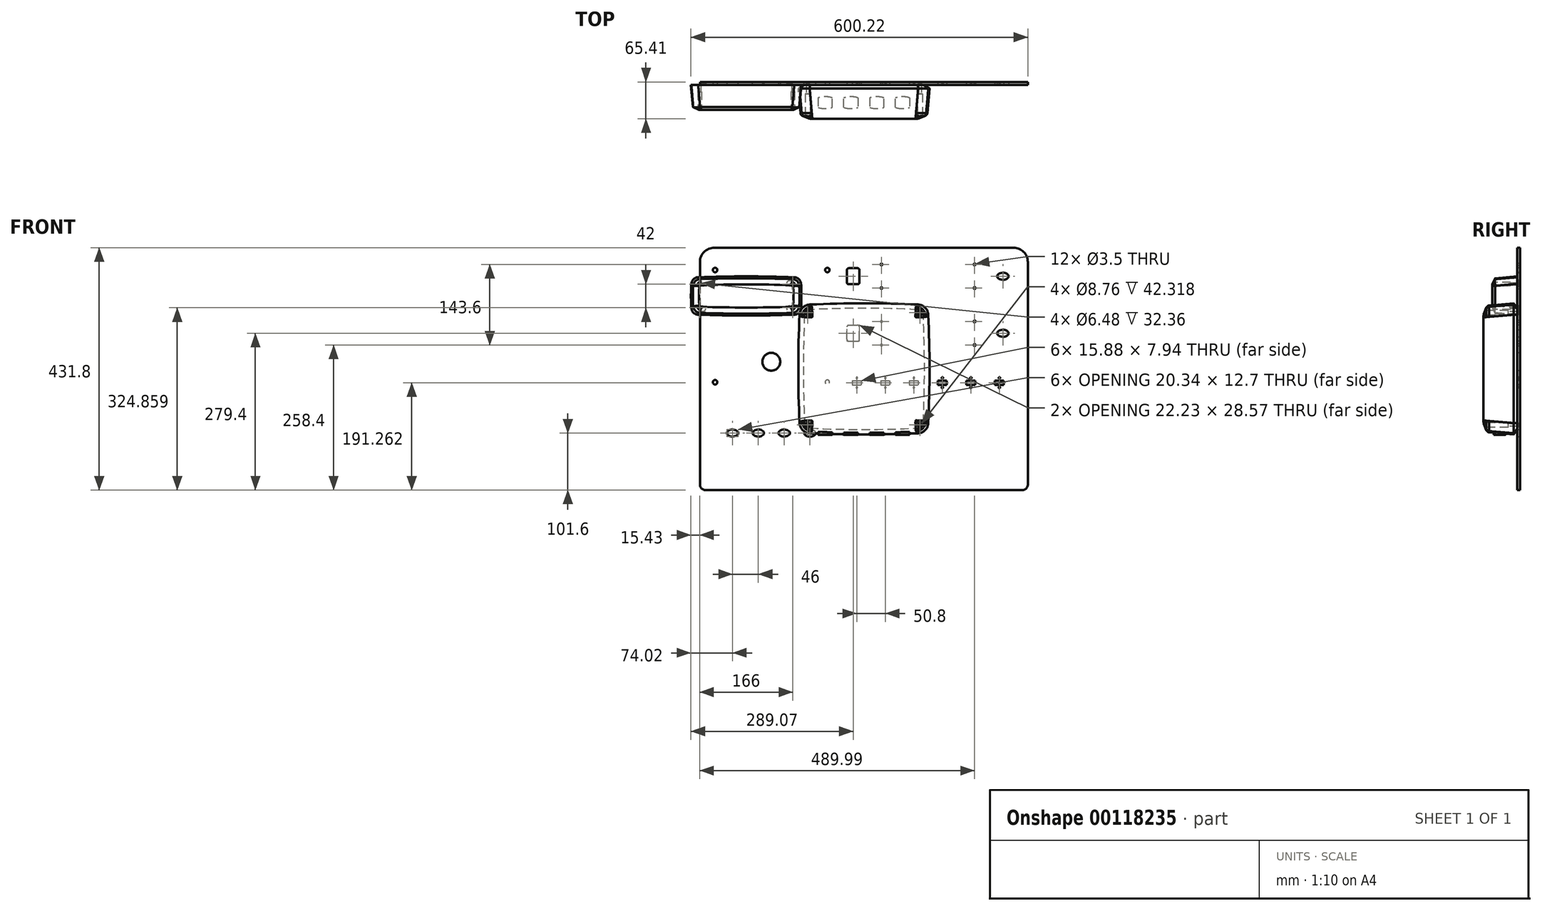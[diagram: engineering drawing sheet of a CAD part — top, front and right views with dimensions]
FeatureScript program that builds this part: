
annotation { "Feature Type Name" : "Feature", "Feature Type Description" : "" }
export const myFeature = defineFeature(function(context is Context, id is Id, definition is map)
    precondition{}
    {
        {
            var Q0;
            Q0=qCreatedBy(makeId("Front.planeOp"),FACE);
            var sketch = newSketch(context, id + "F0", { "sketchPlane" : qUnion([Q0])});
            skLineSegment(sketch, "E0.bottom", {"start": v(-117.48, 117.47) * mm, "end": v(117.48, 117.47) * mm, "construction": true});
            skLineSegment(sketch, "E0.top", {"start": v(-117.48, -117.47) * mm, "end": v(117.48, -117.47) * mm, "construction": true});
            skLineSegment(sketch, "E0.left", {"start": v(-117.48, 117.47) * mm, "end": v(-117.48, -117.47) * mm, "construction": true});
            skLineSegment(sketch, "E0.right", {"start": v(117.48, 117.47) * mm, "end": v(117.48, -117.47) * mm, "construction": true});
            skArc(sketch, "E1", {"start": v(-114.3, 114.3) * mm, "mid": v(-117.48, 0) * mm, "end": v(-114.3, -114.3) * mm});
            skLineSegment(sketch, "E2", {"start": v(0, 93.92) * mm, "end": v(0, -97.92) * mm, "construction": true});
            skLineSegment(sketch, "E3", {"start": v(-172.64, 0) * mm, "end": v(3.6, 0) * mm, "construction": true});
            skArc(sketch, "E4", {"start": v(114.3, 114.3) * mm, "mid": v(0, 117.48) * mm, "end": v(-114.3, 114.3) * mm});
            skArc(sketch, "E5", {"start": v(114.3, -114.3) * mm, "mid": v(117.48, 0) * mm, "end": v(114.3, 114.3) * mm});
            skArc(sketch, "E6", {"start": v(-114.3, -114.3) * mm, "mid": v(0, -117.48) * mm, "end": v(114.3, -114.3) * mm});
            skSolve(sketch);
        }
        {
            var Q0;
            Q0=makeQuery(id+"F0.imprint","IMPRINT",FACE,{"disambiguationData":[TD([[makeQuery(id+"F0.imprint","IMPRINT",EDGE,{"derivedFrom":sQuery(id+"F0.wireOp",EDGE,"E1")}),1.0]])]});
            extrude(context, id + "F1", {"entities" : qUnion([Q0]), "depth" : 60.32 * mm, "hasDraft" : true, "draftAngle" : 5 * degree, "draftPullDirection" : true});
        }
        {
            var Q0;
            Q0=makeQuery(id+"F1.opExtrude","SWEPT_EDGE",EDGE,{"disambiguationData":[OSD([sQuery(id+"F0.wireOp",EDGE,"E1"),sQuery(id+"F0.wireOp",EDGE,"E4")])]});
            var Q1;
            Q1=makeQuery(id+"F1.opExtrude","SWEPT_EDGE",EDGE,{"disambiguationData":[OSD([sQuery(id+"F0.wireOp",EDGE,"E4"),sQuery(id+"F0.wireOp",EDGE,"E5")])]});
            var Q2;
            Q2=makeQuery(id+"F1.opExtrude","SWEPT_EDGE",EDGE,{"disambiguationData":[OSD([sQuery(id+"F0.wireOp",EDGE,"E5"),sQuery(id+"F0.wireOp",EDGE,"E6")])]});
            var Q3;
            Q3=makeQuery(id+"F1.opExtrude","SWEPT_EDGE",EDGE,{"disambiguationData":[OSD([sQuery(id+"F0.wireOp",EDGE,"E1"),sQuery(id+"F0.wireOp",EDGE,"E6")])]});
            fillet(context, id + "F2", {"entities" : qUnion([Q0, Q1, Q2, Q3]), "radius" : 19.05 * mm, "tangentPropagation" : true, "allowEdgeOverflow" : false});
        }
        {
            var Q0;
            Q0=makeQuery(id+"F1.opExtrude","CAP_EDGE",EDGE,{"disambiguationData":[OSD([sQuery(id+"F0.wireOp",EDGE,"E6")])],"isStart":false});
            chamfer(context, id + "F3", {"entities" : qUnion([Q0]), "chamferType" : ChamferType.TWO_OFFSETS, "width1" : 15.88 * mm, "oppositeDirection" : false, "width2" : 6.35 * mm, "tangentPropagation" : true});
        }
        {
            var Q0;
            Q0=makeQuery(id+"F1.opExtrude","CAP_FACE",FACE,{"disambiguationData":[OSD([sQuery(id+"F0.wireOp",EDGE,"E1"),sQuery(id+"F0.wireOp",EDGE,"E4"),sQuery(id+"F0.wireOp",EDGE,"E5"),sQuery(id+"F0.wireOp",EDGE,"E6")])],"isStart":true});
            chamfer(context, id + "F4", {"entities" : qUnion([Q0]), "chamferType" : ChamferType.TWO_OFFSETS, "width1" : 9.52 * mm, "oppositeDirection" : false, "width2" : 6.35 * mm, "tangentPropagation" : true});
        }
        {
            var Q0;
            Q0=makeQuery(id+"F1.opExtrude","CAP_FACE",FACE,{"disambiguationData":[OSD([sQuery(id+"F0.wireOp",EDGE,"E1"),sQuery(id+"F0.wireOp",EDGE,"E4"),sQuery(id+"F0.wireOp",EDGE,"E5"),sQuery(id+"F0.wireOp",EDGE,"E6")])],"isStart":false});
            fillet(context, id + "F5", {"entities" : qUnion([Q0]), "radius" : 9.52 * mm, "tangentPropagation" : true, "allowEdgeOverflow" : false});
        }
        {
            var Q0;
            {var subQ0=sQuery(id+"F0.wireOp",EDGE,"E1");Q0=makeQuery(id+"F3.opChamfer","BLEND_EDGE",EDGE,{"blendedFrom":[makeQuery(id+"F1.opExtrude","CAP_EDGE",EDGE,{"disambiguationData":[OSD([subQ0])],"isStart":false}),makeQuery(id+"F1.opExtrude","SWEPT_FACE",FACE,{"disambiguationData":[OSD([subQ0])]})],"blendedInto":[makeQuery(id+"F1.opExtrude","SWEPT_FACE",FACE,{"disambiguationData":[OSD([subQ0])]})]});}
            var Q1;
            {var subQ0=sQuery(id+"F0.wireOp",EDGE,"E4");var subQ1=sQuery(id+"F0.wireOp",EDGE,"E1");Q1=makeQuery(id+"F3.opChamfer","BLEND_EDGE",EDGE,{"blendedFrom":[makeQuery(id+"F2.opFillet","BLEND_EDGE",EDGE,{"blendedFrom":[makeQuery(id+"F1.opExtrude","SWEPT_EDGE",EDGE,{"disambiguationData":[OSD([subQ1,subQ0])]}),makeQuery(id+"F1.opExtrude","CAP_FACE",FACE,{"disambiguationData":[OSD([subQ1,subQ0,sQuery(id+"F0.wireOp",EDGE,"E5"),sQuery(id+"F0.wireOp",EDGE,"E6")])],"isStart":false})],"blendedInto":[makeQuery(id+"F1.opExtrude","CAP_FACE",FACE,{"disambiguationData":[OSD([subQ1,subQ0,sQuery(id+"F0.wireOp",EDGE,"E5"),sQuery(id+"F0.wireOp",EDGE,"E6")])],"isStart":false})]}),makeQuery(id+"F2.opFillet","BLEND_FACE",FACE,{"disambiguationData":[OSD([subQ1,subQ0])]})],"blendedInto":[makeQuery(id+"F2.opFillet","BLEND_FACE",FACE,{"disambiguationData":[OSD([subQ1,subQ0])]})]});}
            var Q2;
            {var subQ0=sQuery(id+"F0.wireOp",EDGE,"E4");Q2=makeQuery(id+"F3.opChamfer","BLEND_EDGE",EDGE,{"blendedFrom":[makeQuery(id+"F1.opExtrude","CAP_EDGE",EDGE,{"disambiguationData":[OSD([subQ0])],"isStart":false}),makeQuery(id+"F1.opExtrude","SWEPT_FACE",FACE,{"disambiguationData":[OSD([subQ0])]})],"blendedInto":[makeQuery(id+"F1.opExtrude","SWEPT_FACE",FACE,{"disambiguationData":[OSD([subQ0])]})]});}
            var Q3;
            {var subQ0=sQuery(id+"F0.wireOp",EDGE,"E6");var subQ1=sQuery(id+"F0.wireOp",EDGE,"E1");Q3=makeQuery(id+"F3.opChamfer","BLEND_EDGE",EDGE,{"blendedFrom":[makeQuery(id+"F2.opFillet","BLEND_EDGE",EDGE,{"blendedFrom":[makeQuery(id+"F1.opExtrude","SWEPT_EDGE",EDGE,{"disambiguationData":[OSD([subQ1,subQ0])]}),makeQuery(id+"F1.opExtrude","CAP_FACE",FACE,{"disambiguationData":[OSD([subQ1,sQuery(id+"F0.wireOp",EDGE,"E4"),sQuery(id+"F0.wireOp",EDGE,"E5"),subQ0])],"isStart":false})],"blendedInto":[makeQuery(id+"F1.opExtrude","CAP_FACE",FACE,{"disambiguationData":[OSD([subQ1,sQuery(id+"F0.wireOp",EDGE,"E4"),sQuery(id+"F0.wireOp",EDGE,"E5"),subQ0])],"isStart":false})]}),makeQuery(id+"F2.opFillet","BLEND_FACE",FACE,{"disambiguationData":[OSD([subQ1,subQ0])]})],"blendedInto":[makeQuery(id+"F2.opFillet","BLEND_FACE",FACE,{"disambiguationData":[OSD([subQ1,subQ0])]})]});}
            var Q4;
            {var subQ0=sQuery(id+"F0.wireOp",EDGE,"E6");Q4=makeQuery(id+"F3.opChamfer","BLEND_EDGE",EDGE,{"blendedFrom":[makeQuery(id+"F1.opExtrude","CAP_EDGE",EDGE,{"disambiguationData":[OSD([subQ0])],"isStart":false}),makeQuery(id+"F1.opExtrude","SWEPT_FACE",FACE,{"disambiguationData":[OSD([subQ0])]})],"blendedInto":[makeQuery(id+"F1.opExtrude","SWEPT_FACE",FACE,{"disambiguationData":[OSD([subQ0])]})]});}
            var Q5;
            {var subQ0=sQuery(id+"F0.wireOp",EDGE,"E6");var subQ1=sQuery(id+"F0.wireOp",EDGE,"E5");Q5=makeQuery(id+"F3.opChamfer","BLEND_EDGE",EDGE,{"blendedFrom":[makeQuery(id+"F2.opFillet","BLEND_EDGE",EDGE,{"blendedFrom":[makeQuery(id+"F1.opExtrude","SWEPT_EDGE",EDGE,{"disambiguationData":[OSD([subQ1,subQ0])]}),makeQuery(id+"F1.opExtrude","CAP_FACE",FACE,{"disambiguationData":[OSD([sQuery(id+"F0.wireOp",EDGE,"E1"),sQuery(id+"F0.wireOp",EDGE,"E4"),subQ1,subQ0])],"isStart":false})],"blendedInto":[makeQuery(id+"F1.opExtrude","CAP_FACE",FACE,{"disambiguationData":[OSD([sQuery(id+"F0.wireOp",EDGE,"E1"),sQuery(id+"F0.wireOp",EDGE,"E4"),subQ1,subQ0])],"isStart":false})]}),makeQuery(id+"F2.opFillet","BLEND_FACE",FACE,{"disambiguationData":[OSD([subQ1,subQ0])]})],"blendedInto":[makeQuery(id+"F2.opFillet","BLEND_FACE",FACE,{"disambiguationData":[OSD([subQ1,subQ0])]})]});}
            var Q6;
            {var subQ0=sQuery(id+"F0.wireOp",EDGE,"E5");Q6=makeQuery(id+"F3.opChamfer","BLEND_EDGE",EDGE,{"blendedFrom":[makeQuery(id+"F1.opExtrude","CAP_EDGE",EDGE,{"disambiguationData":[OSD([subQ0])],"isStart":false}),makeQuery(id+"F1.opExtrude","SWEPT_FACE",FACE,{"disambiguationData":[OSD([subQ0])]})],"blendedInto":[makeQuery(id+"F1.opExtrude","SWEPT_FACE",FACE,{"disambiguationData":[OSD([subQ0])]})]});}
            var Q7;
            {var subQ0=sQuery(id+"F0.wireOp",EDGE,"E5");var subQ1=sQuery(id+"F0.wireOp",EDGE,"E4");Q7=makeQuery(id+"F3.opChamfer","BLEND_EDGE",EDGE,{"blendedFrom":[makeQuery(id+"F2.opFillet","BLEND_EDGE",EDGE,{"blendedFrom":[makeQuery(id+"F1.opExtrude","SWEPT_EDGE",EDGE,{"disambiguationData":[OSD([subQ1,subQ0])]}),makeQuery(id+"F1.opExtrude","CAP_FACE",FACE,{"disambiguationData":[OSD([sQuery(id+"F0.wireOp",EDGE,"E1"),subQ1,subQ0,sQuery(id+"F0.wireOp",EDGE,"E6")])],"isStart":false})],"blendedInto":[makeQuery(id+"F1.opExtrude","CAP_FACE",FACE,{"disambiguationData":[OSD([sQuery(id+"F0.wireOp",EDGE,"E1"),subQ1,subQ0,sQuery(id+"F0.wireOp",EDGE,"E6")])],"isStart":false})]}),makeQuery(id+"F2.opFillet","BLEND_FACE",FACE,{"disambiguationData":[OSD([subQ1,subQ0])]})],"blendedInto":[makeQuery(id+"F2.opFillet","BLEND_FACE",FACE,{"disambiguationData":[OSD([subQ1,subQ0])]})]});}
            fillet(context, id + "F6", {"entities" : qUnion([Q0, Q1, Q2, Q3, Q4, Q5, Q6, Q7]), "radius" : 6.35 * mm, "tangentPropagation" : true, "allowEdgeOverflow" : false});
        }
        {
            var Q0;
            Q0=makeQuery(id+"F1.opExtrude","CAP_FACE",FACE,{"disambiguationData":[OSD([sQuery(id+"F0.wireOp",EDGE,"E1"),sQuery(id+"F0.wireOp",EDGE,"E4"),sQuery(id+"F0.wireOp",EDGE,"E5"),sQuery(id+"F0.wireOp",EDGE,"E6")])],"isStart":true});
            var sketch = newSketch(context, id + "F7", { "sketchPlane" : qUnion([Q0])});
            skLineSegment(sketch, "E7.bottom", {"start": v(100, -100) * mm, "end": v(-100, -100) * mm, "construction": true});
            skLineSegment(sketch, "E7.top", {"start": v(100, 100) * mm, "end": v(-100, 100) * mm, "construction": true});
            skLineSegment(sketch, "E7.left", {"start": v(100, -100) * mm, "end": v(100, 100) * mm, "construction": true});
            skLineSegment(sketch, "E7.right", {"start": v(-100, -100) * mm, "end": v(-100, 100) * mm, "construction": true});
            skLineSegment(sketch, "E8", {"start": v(107.95, 0) * mm, "end": v(-107.95, 0) * mm, "construction": true});
            skLineSegment(sketch, "E9", {"start": v(0, -107.95) * mm, "end": v(0, 107.95) * mm, "construction": true});
            skCircle(sketch, "E10", {"center": v(100, 100) * mm, "radius": 3.97 * mm});
            skCircle(sketch, "E11", {"center": v(-100, 100) * mm, "radius": 3.97 * mm});
            skCircle(sketch, "E12", {"center": v(100, -100) * mm, "radius": 3.97 * mm});
            skCircle(sketch, "E13", {"center": v(-100, -100) * mm, "radius": 3.97 * mm});
            skSolve(sketch);
        }
        {
            var Q0;
            Q0 = qSketchRegion(id + "F7", true);
            extrude(context, id + "F8", {"entities" : qUnion([Q0]), "operationType" : NewBodyOperationType.ADD, "depth" : 1.59 * mm});
        }
        {
            var Q0;
            Q0=makeQuery(id+"F1.opExtrude","CAP_FACE",FACE,{"disambiguationData":[OSD([sQuery(id+"F0.wireOp",EDGE,"E1"),sQuery(id+"F0.wireOp",EDGE,"E4"),sQuery(id+"F0.wireOp",EDGE,"E5"),sQuery(id+"F0.wireOp",EDGE,"E6")])],"isStart":false});
            var sketch = newSketch(context, id + "F9", { "sketchPlane" : qUnion([Q0])});
            skPoint(sketch, "E14.0", {"position": v(-100, 100) * mm});
            skPoint(sketch, "E15.0", {"position": v(-100, -100) * mm});
            skPoint(sketch, "E16.0", {"position": v(100, 100) * mm});
            skPoint(sketch, "E17.0", {"position": v(100, -100) * mm});
            skSolve(sketch);
        }
        {
            var Q0;
            Q0=sQuery(id+"F9.wireOp",VERTEX,"E14.0");
            var Q1;
            Q1=sQuery(id+"F9.wireOp",VERTEX,"E15.0");
            var Q2;
            Q2=sQuery(id+"F9.wireOp",VERTEX,"E16.0");
            var Q3;
            Q3=sQuery(id+"F9.wireOp",VERTEX,"E17.0");
            var Q4;
            Q4=makeQuery(id+"F1.opExtrude","SWEPT_BODY",BODY,{"disambiguationData":[OSD([sQuery(id+"F0.wireOp",EDGE,"E1"),sQuery(id+"F0.wireOp",EDGE,"E4"),sQuery(id+"F0.wireOp",EDGE,"E5"),sQuery(id+"F0.wireOp",EDGE,"E6")])]});
            hole(context, id + "F10", {"style" : HoleStyle.C_BORE, "endStyle" : HoleEndStyle.THROUGH, "holeDiameter" : 4.83 * mm, "cBoreDiameter" : 8.76 * mm, "cBoreDepth" : 39.12 * mm, "locations" : qUnion([Q0, Q1, Q2, Q3]), "scope" : qUnion([Q4]), "isTappedThrough" : true});
        }
        {
            var Q0;
            Q0=qCreatedBy(makeId("Top.planeOp"),FACE);
            var sketch = newSketch(context, id + "F11", { "sketchPlane" : qUnion([Q0])});
            skLineSegment(sketch, "E18", {"start": v(-81.7, -23.3) * mm, "end": v(-81.7, -40.2) * mm});
            skArc(sketch, "E19", {"start": v(-81.7, -40.2) * mm, "mid": v(-69, -42.39) * mm, "end": v(-56.3, -40.2) * mm});
            skArc(sketch, "E20", {"start": v(-56.3, -23.3) * mm, "mid": v(-69, -21.11) * mm, "end": v(-81.7, -23.3) * mm});
            skLineSegment(sketch, "E21", {"start": v(-56.3, -40.2) * mm, "end": v(-56.3, -23.3) * mm});
            skLineSegment(sketch, "E22", {"start": v(-69, -88.01) * mm, "end": v(-69, 60.18) * mm, "construction": true});
            skLineSegment(sketch, "E23", {"start": v(-113.39, -31.75) * mm, "end": v(-52.19, -31.75) * mm, "construction": true});
            skPoint(sketch, "E23.startSnap0", {"position": v(-81.7, -31.75) * mm});
            skLineSegment(sketch, "E24", {"start": v(-46, -94.56) * mm, "end": v(-46, 70.5) * mm, "construction": true});
            skArc(sketch, "E25.MirrorCS", {"start": v(-10.3, -40.2) * mm, "mid": v(-23, -42.39) * mm, "end": v(-35.7, -40.2) * mm});
            skLineSegment(sketch, "E26.MirrorCS", {"start": v(-10.3, -23.3) * mm, "end": v(-10.3, -40.2) * mm});
            skArc(sketch, "E27.MirrorCS", {"start": v(-35.7, -23.3) * mm, "mid": v(-23, -21.11) * mm, "end": v(-10.3, -23.3) * mm});
            skLineSegment(sketch, "E28.MirrorCS", {"start": v(-35.7, -40.2) * mm, "end": v(-35.7, -23.3) * mm});
            skLineSegment(sketch, "E29.MirrorCS", {"start": v(-23, -88.01) * mm, "end": v(-23, 60.18) * mm, "construction": true});
            skLineSegment(sketch, "E30", {"start": v(0, 14.2) * mm, "end": v(0, 67.5) * mm, "construction": true});
            skArc(sketch, "E31.MirrorCS", {"start": v(81.7, -40.2) * mm, "mid": v(69, -42.39) * mm, "end": v(56.3, -40.2) * mm});
            skLineSegment(sketch, "E32.MirrorCS", {"start": v(81.7, -23.3) * mm, "end": v(81.7, -40.2) * mm});
            skArc(sketch, "E33.MirrorCS", {"start": v(56.3, -23.3) * mm, "mid": v(69, -21.11) * mm, "end": v(81.7, -23.3) * mm});
            skLineSegment(sketch, "E34.MirrorCS", {"start": v(56.3, -40.2) * mm, "end": v(56.3, -23.3) * mm});
            skArc(sketch, "E35.MirrorCS", {"start": v(10.3, -40.2) * mm, "mid": v(23, -42.39) * mm, "end": v(35.7, -40.2) * mm});
            skLineSegment(sketch, "E36.MirrorCS", {"start": v(35.7, -40.2) * mm, "end": v(35.7, -23.3) * mm});
            skArc(sketch, "E37.MirrorCS", {"start": v(35.7, -23.3) * mm, "mid": v(23, -21.11) * mm, "end": v(10.3, -23.3) * mm});
            skLineSegment(sketch, "E38.MirrorCS", {"start": v(10.3, -23.3) * mm, "end": v(10.3, -40.2) * mm});
            skLineSegment(sketch, "E39.MirrorCS", {"start": v(23, -88.01) * mm, "end": v(23, 60.18) * mm, "construction": true});
            skSolve(sketch);
        }
        {
            var Q0;
            Q0 = qSketchRegion(id + "F11", true);
            extrude(context, id + "F12", {"entities" : qUnion([Q0]), "operationType" : NewBodyOperationType.ADD, "oppositeDirection" : true, "depth" : 117.47 * mm});
        }
        {
            var Q0;
            Q0=qCreatedBy(makeId("Front.planeOp"),FACE);
            var sketch = newSketch(context, id + "F13", { "sketchPlane" : qUnion([Q0])});
            skLineSegment(sketch, "E40.bottom", {"start": v(-308.12, 164.88) * mm, "end": v(-111.27, 164.88) * mm, "construction": true});
            skLineSegment(sketch, "E40.top", {"start": v(-308.12, 95.03) * mm, "end": v(-111.27, 95.03) * mm, "construction": true});
            skLineSegment(sketch, "E40.left", {"start": v(-308.12, 164.88) * mm, "end": v(-308.12, 95.03) * mm, "construction": true});
            skLineSegment(sketch, "E40.right", {"start": v(-111.27, 164.88) * mm, "end": v(-111.27, 95.03) * mm, "construction": true});
            skArc(sketch, "E41", {"start": v(-306.53, 162.98) * mm, "mid": v(-308.12, 129.96) * mm, "end": v(-306.53, 96.94) * mm});
            skLineSegment(sketch, "E42", {"start": v(-209.7, 113.79) * mm, "end": v(-209.7, -78.05) * mm, "construction": true});
            skLineSegment(sketch, "E43", {"start": v(-401.38, 129.96) * mm, "end": v(-225.14, 129.96) * mm, "construction": true});
            skArc(sketch, "E44", {"start": v(-112.85, 162.98) * mm, "mid": v(-209.7, 164.88) * mm, "end": v(-306.53, 162.98) * mm});
            skArc(sketch, "E45", {"start": v(-112.85, 96.94) * mm, "mid": v(-111.27, 129.96) * mm, "end": v(-112.85, 162.98) * mm});
            skArc(sketch, "E46", {"start": v(-306.53, 96.94) * mm, "mid": v(-209.7, 95.03) * mm, "end": v(-112.85, 96.94) * mm});
            skSolve(sketch);
        }
        {
            var Q0;
            Q0=makeQuery(id+"F13.imprint","IMPRINT",FACE,{"disambiguationData":[TD([[makeQuery(id+"F13.imprint","IMPRINT",EDGE,{"derivedFrom":sQuery(id+"F13.wireOp",EDGE,"E41")}),1.0]])]});
            extrude(context, id + "F14", {"entities" : qUnion([Q0]), "depth" : 44.45 * mm, "hasDraft" : true, "draftAngle" : 5 * degree, "draftPullDirection" : true});
        }
        {
            var Q0;
            Q0=makeQuery(id+"F14.opExtrude","SWEPT_EDGE",EDGE,{"disambiguationData":[OSD([sQuery(id+"F13.wireOp",EDGE,"E44"),sQuery(id+"F13.wireOp",EDGE,"E45")])]});
            var Q1;
            Q1=makeQuery(id+"F14.opExtrude","SWEPT_EDGE",EDGE,{"disambiguationData":[OSD([sQuery(id+"F13.wireOp",EDGE,"E41"),sQuery(id+"F13.wireOp",EDGE,"E44")])]});
            var Q2;
            Q2=makeQuery(id+"F14.opExtrude","SWEPT_EDGE",EDGE,{"disambiguationData":[OSD([sQuery(id+"F13.wireOp",EDGE,"E41"),sQuery(id+"F13.wireOp",EDGE,"E46")])]});
            var Q3;
            Q3=makeQuery(id+"F14.opExtrude","SWEPT_EDGE",EDGE,{"disambiguationData":[OSD([sQuery(id+"F13.wireOp",EDGE,"E45"),sQuery(id+"F13.wireOp",EDGE,"E46")])]});
            fillet(context, id + "F15", {"entities" : qUnion([Q0, Q1, Q2, Q3]), "radius" : 12.7 * mm, "tangentPropagation" : true, "allowEdgeOverflow" : false});
        }
        {
            var Q0;
            Q0=makeQuery(id+"F14.opExtrude","CAP_EDGE",EDGE,{"disambiguationData":[OSD([sQuery(id+"F13.wireOp",EDGE,"E46")])],"isStart":false});
            chamfer(context, id + "F16", {"entities" : qUnion([Q0]), "chamferType" : ChamferType.TWO_OFFSETS, "width1" : 10.48 * mm, "oppositeDirection" : false, "width2" : 4.76 * mm, "tangentPropagation" : true});
        }
        {
            var Q0;
            Q0=makeQuery(id+"F14.opExtrude","CAP_FACE",FACE,{"disambiguationData":[OSD([sQuery(id+"F13.wireOp",EDGE,"E41"),sQuery(id+"F13.wireOp",EDGE,"E44"),sQuery(id+"F13.wireOp",EDGE,"E45"),sQuery(id+"F13.wireOp",EDGE,"E46")])],"isStart":true});
            var sketch = newSketch(context, id + "F17", { "sketchPlane" : qUnion([Q0])});
            skLineSegment(sketch, "E47", {"start": v(209.7, 164.88) * mm, "end": v(209.7, 95.03) * mm, "construction": true});
            skLineSegment(sketch, "E48", {"start": v(111.27, 129.96) * mm, "end": v(308.12, 129.96) * mm, "construction": true});
            skCircle(sketch, "E49", {"center": v(132.7, 152.46) * mm, "radius": 4.76 * mm});
            skCircle(sketch, "E50.MirrorC", {"center": v(286.7, 152.46) * mm, "radius": 4.76 * mm});
            skCircle(sketch, "E51.MirrorC", {"center": v(132.7, 107.46) * mm, "radius": 4.76 * mm});
            skCircle(sketch, "E52.MirrorC", {"center": v(286.7, 107.46) * mm, "radius": 4.76 * mm});
            skSolve(sketch);
        }
        {
            var Q0;
            Q0 = qSketchRegion(id + "F17", true);
            extrude(context, id + "F18", {"entities" : qUnion([Q0]), "operationType" : NewBodyOperationType.ADD, "depth" : 2.7 * mm});
        }
        {
            var Q0;
            Q0=makeQuery(id+"F14.opExtrude","CAP_FACE",FACE,{"disambiguationData":[OSD([sQuery(id+"F13.wireOp",EDGE,"E41"),sQuery(id+"F13.wireOp",EDGE,"E44"),sQuery(id+"F13.wireOp",EDGE,"E45"),sQuery(id+"F13.wireOp",EDGE,"E46")])],"isStart":false});
            var sketch = newSketch(context, id + "F19", { "sketchPlane" : qUnion([Q0])});
            skLineSegment(sketch, "E53", {"start": v(-209.7, 150.52) * mm, "end": v(-209.7, 109.4) * mm, "construction": true});
            skLineSegment(sketch, "E54", {"start": v(-293.75, 129.96) * mm, "end": v(-125.63, 129.96) * mm, "construction": true});
            skPoint(sketch, "E55", {"position": v(-292.7, 150.96) * mm});
            skPoint(sketch, "E56.MirrorP", {"position": v(-126.7, 150.96) * mm});
            skPoint(sketch, "E57.MirrorP", {"position": v(-292.7, 108.96) * mm});
            skPoint(sketch, "E58.MirrorP", {"position": v(-126.7, 108.96) * mm});
            skSolve(sketch);
        }
        {
            var Q0;
            Q0=sQuery(id+"F19.wireOp",VERTEX,"E55");
            var Q1;
            Q1=sQuery(id+"F19.wireOp",VERTEX,"E57.MirrorP");
            var Q2;
            Q2=sQuery(id+"F19.wireOp",VERTEX,"E56.MirrorP");
            var Q3;
            Q3=sQuery(id+"F19.wireOp",VERTEX,"E58.MirrorP");
            var Q4;
            Q4=makeQuery(id+"F14.opExtrude","SWEPT_BODY",BODY,{"disambiguationData":[OSD([sQuery(id+"F13.wireOp",EDGE,"E41"),sQuery(id+"F13.wireOp",EDGE,"E44"),sQuery(id+"F13.wireOp",EDGE,"E45"),sQuery(id+"F13.wireOp",EDGE,"E46")])]});
            hole(context, id + "F20", {"style" : HoleStyle.C_BORE, "endStyle" : HoleEndStyle.THROUGH, "holeDiameter" : 3.5 * mm, "cBoreDiameter" : 6.48 * mm, "cBoreDepth" : 30.16 * mm, "locations" : qUnion([Q0, Q1, Q2, Q3]), "scope" : qUnion([Q4]), "isTappedThrough" : true});
        }
        {
            var Q0;
            Q0=qCreatedBy(makeId("Front.planeOp"),FACE);
            var sketch = newSketch(context, id + "F21", { "sketchPlane" : qUnion([Q0])});
            skLineSegment(sketch, "E59.bottom", {"start": v(-292.1, 215.9) * mm, "end": v(292.1, 215.9) * mm});
            skLineSegment(sketch, "E59.top", {"start": v(-292.1, -215.9) * mm, "end": v(292.1, -215.9) * mm});
            skLineSegment(sketch, "E59.left", {"start": v(-292.1, 215.9) * mm, "end": v(-292.1, -215.9) * mm});
            skLineSegment(sketch, "E59.right", {"start": v(292.1, 215.9) * mm, "end": v(292.1, -215.9) * mm});
            skSolve(sketch);
        }
        {
            var Q0;
            Q0=makeQuery(id+"F21.imprint","IMPRINT",FACE,{"disambiguationData":[TD([[makeQuery(id+"F21.imprint","IMPRINT",EDGE,{"derivedFrom":sQuery(id+"F21.wireOp",EDGE,"E59.bottom")}),-1.0]])]});
            extrude(context, id + "F22", {"entities" : qUnion([Q0]), "oppositeDirection" : true, "depth" : 5.08 * mm});
        }
        {
            var Q0;
            Q0=makeQuery(id+"F22.opExtrude","CAP_FACE",FACE,{"disambiguationData":[OSD([sQuery(id+"F21.wireOp",EDGE,"E59.bottom"),sQuery(id+"F21.wireOp",EDGE,"E59.top"),sQuery(id+"F21.wireOp",EDGE,"E59.left"),sQuery(id+"F21.wireOp",EDGE,"E59.right")])],"isStart":true});
            var sketch = newSketch(context, id + "F23", { "sketchPlane" : qUnion([Q0])});
            skLineSegment(sketch, "E60", {"start": v(-165.1, 279.4) * mm, "end": v(-165.1, -77.11) * mm, "construction": true});
            skLineSegment(sketch, "E61", {"start": v(-76.57, 76.2) * mm, "end": v(108.75, 76.2) * mm, "construction": true});
            skLineSegment(sketch, "E62", {"start": v(120.05, 165.1) * mm, "end": v(312.45, 165.1) * mm, "construction": true});
            skLineSegment(sketch, "E63", {"start": v(-87.1, 114.3) * mm, "end": v(113.98, 114.3) * mm, "construction": true});
            skCircle(sketch, "E64", {"center": v(-265.1, 176.2) * mm, "radius": 3.97 * mm});
            skCircle(sketch, "E65", {"center": v(31.3, 186.1) * mm, "radius": 1.75 * mm});
            skCircle(sketch, "E66.MirrorC", {"center": v(-65.1, 176.2) * mm, "radius": 3.97 * mm});
            skCircle(sketch, "E67.MirrorC", {"center": v(197.3, 186.1) * mm, "radius": 1.75 * mm});
            skCircle(sketch, "E68.MirrorC", {"center": v(-265.1, -23.8) * mm, "radius": 3.97 * mm});
            skCircle(sketch, "E69.MirrorC", {"center": v(-65.1, -23.8) * mm, "radius": 3.97 * mm});
            skCircle(sketch, "E70.MirrorC", {"center": v(31.3, 144.1) * mm, "radius": 1.75 * mm});
            skCircle(sketch, "E71.MirrorC", {"center": v(197.3, 144.1) * mm, "radius": 1.75 * mm});
            skCircle(sketch, "E72.MirrorC", {"center": v(31.3, 84.5) * mm, "radius": 1.75 * mm});
            skCircle(sketch, "E73.MirrorC", {"center": v(31.3, 42.5) * mm, "radius": 1.75 * mm});
            skCircle(sketch, "E74.MirrorC", {"center": v(197.3, 42.5) * mm, "radius": 1.75 * mm});
            skCircle(sketch, "E75.MirrorC", {"center": v(197.3, 84.5) * mm, "radius": 1.75 * mm});
            skCircle(sketch, "E76", {"center": v(-165.1, 12.7) * mm, "radius": 15.88 * mm});
            skLineSegment(sketch, "E77.bottom", {"start": v(-196.04, -110.33) * mm, "end": v(-180.16, -110.33) * mm, "construction": true});
            skLineSegment(sketch, "E77.top", {"start": v(-196.04, -118.27) * mm, "end": v(-180.16, -118.27) * mm, "construction": true});
            skLineSegment(sketch, "E77.left", {"start": v(-196.04, -110.33) * mm, "end": v(-196.04, -118.27) * mm, "construction": true});
            skLineSegment(sketch, "E77.right", {"start": v(-180.16, -110.33) * mm, "end": v(-180.16, -118.27) * mm, "construction": true});
            skLineSegment(sketch, "E78", {"start": v(-188.1, -110.33) * mm, "end": v(-188.1, -118.27) * mm, "construction": true});
            skLineSegment(sketch, "E79", {"start": v(-196.04, -114.3) * mm, "end": v(-180.16, -114.3) * mm, "construction": true});
            skEllipse(sketch, "E80", {"center": v(-188.1, -114.3) * mm, "majorRadius": 10.17 * mm, "minorRadius": 6.35 * mm, "majorAxis": v(1, 0)});
            skLineSegment(sketch, "E81", {"start": v(-211.1, -39.7) * mm, "end": v(-211.1, -73.83) * mm, "construction": true});
            skEllipse(sketch, "E82.MirrorC", {"center": v(-234.1, -114.3) * mm, "majorRadius": 10.17 * mm, "minorRadius": 6.35 * mm, "majorAxis": v(-1, 0)});
            skEllipse(sketch, "E83.MirrorC", {"center": v(-142.1, -114.3) * mm, "majorRadius": 10.17 * mm, "minorRadius": 6.35 * mm, "majorAxis": v(-1, 0)});
            skEllipse(sketch, "E84.MirrorC", {"center": v(-96.1, -114.3) * mm, "majorRadius": 10.17 * mm, "minorRadius": 6.35 * mm, "majorAxis": v(1, 0)});
            skEllipse(sketch, "E85", {"center": v(247.65, 165.1) * mm, "majorRadius": 10.17 * mm, "minorRadius": 6.35 * mm, "majorAxis": v(1, 0)});
            skLineSegment(sketch, "E86.bottom", {"start": v(239.71, 169.07) * mm, "end": v(255.59, 169.07) * mm, "construction": true});
            skLineSegment(sketch, "E86.top", {"start": v(239.71, 161.13) * mm, "end": v(255.59, 161.13) * mm, "construction": true});
            skLineSegment(sketch, "E86.left", {"start": v(239.71, 169.07) * mm, "end": v(239.71, 161.13) * mm, "construction": true});
            skLineSegment(sketch, "E86.right", {"start": v(255.59, 169.07) * mm, "end": v(255.59, 161.13) * mm, "construction": true});
            skLineSegment(sketch, "E87.bottom", {"start": v(-30.16, 179.39) * mm, "end": v(-7.94, 179.39) * mm});
            skLineSegment(sketch, "E87.top", {"start": v(-30.16, 150.81) * mm, "end": v(-7.94, 150.81) * mm});
            skLineSegment(sketch, "E87.left", {"start": v(-30.16, 179.39) * mm, "end": v(-30.16, 150.81) * mm});
            skLineSegment(sketch, "E87.right", {"start": v(-7.94, 179.39) * mm, "end": v(-7.94, 150.81) * mm});
            skPoint(sketch, "E87.middle", {"position": v(-19.05, 165.1) * mm});
            skLineSegment(sketch, "E88.MirrorCS", {"start": v(-30.16, 49.21) * mm, "end": v(-30.16, 77.79) * mm});
            skLineSegment(sketch, "E89.MirrorCS", {"start": v(-30.16, 49.21) * mm, "end": v(-7.94, 49.21) * mm});
            skLineSegment(sketch, "E90.MirrorCS", {"start": v(-7.94, 49.21) * mm, "end": v(-7.94, 77.79) * mm});
            skLineSegment(sketch, "E91.MirrorCS", {"start": v(-30.16, 77.79) * mm, "end": v(-7.94, 77.79) * mm});
            skEllipse(sketch, "E92.MirrorC", {"center": v(247.65, 63.5) * mm, "majorRadius": 10.17 * mm, "minorRadius": 6.35 * mm, "majorAxis": v(1, 0)});
            skLineSegment(sketch, "E93", {"start": v(114.3, 343.9) * mm, "end": v(114.3, -360.95) * mm, "construction": true});
            skSolve(sketch);
        }
        {
            var Q0;
            Q0 = qSketchRegion(id + "F23", true);
            extrude(context, id + "F24", {"entities" : qUnion([Q0]), "operationType" : NewBodyOperationType.REMOVE, "oppositeDirection" : true, "depth" : 25.4 * mm});
        }
        {
            var Q0;
            Q0=makeQuery(id+"F24.boolean.opBoolean","COPY",EDGE,{"derivedFrom":makeQuery(id+"F24.opExtrude","SWEPT_EDGE",EDGE,{"disambiguationData":[OSD([sQuery(id+"F23.wireOp",EDGE,"E87.top"),sQuery(id+"F23.wireOp",EDGE,"E87.left")])]})});
            var Q1;
            Q1=makeQuery(id+"F24.boolean.opBoolean","COPY",EDGE,{"derivedFrom":makeQuery(id+"F24.opExtrude","SWEPT_EDGE",EDGE,{"disambiguationData":[OSD([sQuery(id+"F23.wireOp",EDGE,"E87.bottom"),sQuery(id+"F23.wireOp",EDGE,"E87.left")])]})});
            var Q2;
            Q2=makeQuery(id+"F24.boolean.opBoolean","COPY",EDGE,{"derivedFrom":makeQuery(id+"F24.opExtrude","SWEPT_EDGE",EDGE,{"disambiguationData":[OSD([sQuery(id+"F23.wireOp",EDGE,"E87.bottom"),sQuery(id+"F23.wireOp",EDGE,"E87.right")])]})});
            var Q3;
            Q3=makeQuery(id+"F24.boolean.opBoolean","COPY",EDGE,{"derivedFrom":makeQuery(id+"F24.opExtrude","SWEPT_EDGE",EDGE,{"disambiguationData":[OSD([sQuery(id+"F23.wireOp",EDGE,"E87.top"),sQuery(id+"F23.wireOp",EDGE,"E87.right")])]})});
            var Q4;
            Q4=makeQuery(id+"F24.boolean.opBoolean","COPY",EDGE,{"derivedFrom":makeQuery(id+"F24.opExtrude","SWEPT_EDGE",EDGE,{"disambiguationData":[OSD([sQuery(id+"F23.wireOp",EDGE,"E88.MirrorCS"),sQuery(id+"F23.wireOp",EDGE,"E91.MirrorCS")])]})});
            var Q5;
            Q5=makeQuery(id+"F24.boolean.opBoolean","COPY",EDGE,{"derivedFrom":makeQuery(id+"F24.opExtrude","SWEPT_EDGE",EDGE,{"disambiguationData":[OSD([sQuery(id+"F23.wireOp",EDGE,"E90.MirrorCS"),sQuery(id+"F23.wireOp",EDGE,"E91.MirrorCS")])]})});
            var Q6;
            Q6=makeQuery(id+"F24.boolean.opBoolean","COPY",EDGE,{"derivedFrom":makeQuery(id+"F24.opExtrude","SWEPT_EDGE",EDGE,{"disambiguationData":[OSD([sQuery(id+"F23.wireOp",EDGE,"E89.MirrorCS"),sQuery(id+"F23.wireOp",EDGE,"E90.MirrorCS")])]})});
            var Q7;
            Q7=makeQuery(id+"F24.boolean.opBoolean","COPY",EDGE,{"derivedFrom":makeQuery(id+"F24.opExtrude","SWEPT_EDGE",EDGE,{"disambiguationData":[OSD([sQuery(id+"F23.wireOp",EDGE,"E88.MirrorCS"),sQuery(id+"F23.wireOp",EDGE,"E89.MirrorCS")])]})});
            fillet(context, id + "F25", {"entities" : qUnion([Q0, Q1, Q2, Q3, Q4, Q5, Q6, Q7]), "radius" : 3.17 * mm, "tangentPropagation" : true, "allowEdgeOverflow" : false});
        }
        {
            var Q0;
            Q0=makeQuery(id+"F21.imprint","IMPRINT",FACE,{"disambiguationData":[TD([[makeQuery(id+"F21.imprint","IMPRINT",EDGE,{"derivedFrom":sQuery(id+"F21.wireOp",EDGE,"E59.bottom")}),-1.0]])]});
            var sketch = newSketch(context, id + "F26", { "sketchPlane" : qUnion([Q0])});
            skLineSegment(sketch, "E94.bottom", {"start": v(-20.64, -20.67) * mm, "end": v(-4.76, -20.67) * mm});
            skLineSegment(sketch, "E94.top", {"start": v(-20.64, -28.6) * mm, "end": v(-4.76, -28.6) * mm});
            skLineSegment(sketch, "E94.left", {"start": v(-20.64, -20.67) * mm, "end": v(-20.64, -28.6) * mm});
            skLineSegment(sketch, "E94.right", {"start": v(-4.76, -20.67) * mm, "end": v(-4.76, -28.6) * mm});
            skLineSegment(sketch, "E95", {"start": v(-12.7, -150.26) * mm, "end": v(-12.7, -190.62) * mm, "construction": true});
            skLineSegment(sketch, "E96.bottom", {"start": v(-24.64, -11.18) * mm, "end": v(-0.76, -11.18) * mm, "construction": true});
            skLineSegment(sketch, "E96.top", {"start": v(-24.64, -38.1) * mm, "end": v(-0.76, -38.1) * mm, "construction": true});
            skLineSegment(sketch, "E96.left", {"start": v(-24.64, -11.18) * mm, "end": v(-24.64, -38.1) * mm, "construction": true});
            skLineSegment(sketch, "E96.right", {"start": v(-0.76, -11.18) * mm, "end": v(-0.76, -38.1) * mm, "construction": true});
            skCircle(sketch, "E97", {"center": v(-12.7, -16) * mm, "radius": 1.27 * mm});
            skCircle(sketch, "E98", {"center": v(-12.7, -33.27) * mm, "radius": 1.27 * mm});
            skLineSegment(sketch, "E99", {"start": v(-24.64, -24.64) * mm, "end": v(-0.76, -24.64) * mm, "construction": true});
            skLineSegment(sketch, "E100.1.0.0", {"start": v(26.16, -38.1) * mm, "end": v(50.04, -38.1) * mm, "construction": true});
            skLineSegment(sketch, "E100.1.0.1", {"start": v(50.04, -11.18) * mm, "end": v(50.04, -38.1) * mm, "construction": true});
            skLineSegment(sketch, "E100.1.0.2", {"start": v(26.16, -11.18) * mm, "end": v(50.04, -11.18) * mm, "construction": true});
            skLineSegment(sketch, "E100.1.0.3", {"start": v(26.16, -11.18) * mm, "end": v(26.16, -38.1) * mm, "construction": true});
            skLineSegment(sketch, "E100.1.0.4", {"start": v(30.16, -28.6) * mm, "end": v(46.04, -28.6) * mm});
            skLineSegment(sketch, "E100.1.0.5", {"start": v(46.04, -20.67) * mm, "end": v(46.04, -28.6) * mm});
            skLineSegment(sketch, "E100.1.0.6", {"start": v(30.16, -20.67) * mm, "end": v(46.04, -20.67) * mm});
            skLineSegment(sketch, "E100.1.0.7", {"start": v(30.16, -20.67) * mm, "end": v(30.16, -28.6) * mm});
            skCircle(sketch, "E100.1.0.8", {"center": v(38.1, -33.27) * mm, "radius": 1.27 * mm});
            skCircle(sketch, "E100.1.0.9", {"center": v(38.1, -16) * mm, "radius": 1.27 * mm});
            skLineSegment(sketch, "E100.2.0.0", {"start": v(76.96, -38.1) * mm, "end": v(100.84, -38.1) * mm, "construction": true});
            skLineSegment(sketch, "E100.2.0.1", {"start": v(100.84, -11.18) * mm, "end": v(100.84, -38.1) * mm, "construction": true});
            skLineSegment(sketch, "E100.2.0.2", {"start": v(76.96, -11.18) * mm, "end": v(100.84, -11.18) * mm, "construction": true});
            skLineSegment(sketch, "E100.2.0.3", {"start": v(76.96, -11.18) * mm, "end": v(76.96, -38.1) * mm, "construction": true});
            skLineSegment(sketch, "E100.2.0.4", {"start": v(80.96, -28.6) * mm, "end": v(96.84, -28.6) * mm});
            skLineSegment(sketch, "E100.2.0.5", {"start": v(96.84, -20.67) * mm, "end": v(96.84, -28.6) * mm});
            skLineSegment(sketch, "E100.2.0.6", {"start": v(80.96, -20.67) * mm, "end": v(96.84, -20.67) * mm});
            skLineSegment(sketch, "E100.2.0.7", {"start": v(80.96, -20.67) * mm, "end": v(80.96, -28.6) * mm});
            skCircle(sketch, "E100.2.0.8", {"center": v(88.9, -33.27) * mm, "radius": 1.27 * mm});
            skCircle(sketch, "E100.2.0.9", {"center": v(88.9, -16) * mm, "radius": 1.27 * mm});
            skLineSegment(sketch, "E100.3.0.0", {"start": v(127.76, -38.1) * mm, "end": v(151.64, -38.1) * mm, "construction": true});
            skLineSegment(sketch, "E100.3.0.1", {"start": v(151.64, -11.18) * mm, "end": v(151.64, -38.1) * mm, "construction": true});
            skLineSegment(sketch, "E100.3.0.2", {"start": v(127.76, -11.18) * mm, "end": v(151.64, -11.18) * mm, "construction": true});
            skLineSegment(sketch, "E100.3.0.3", {"start": v(127.76, -11.18) * mm, "end": v(127.76, -38.1) * mm, "construction": true});
            skLineSegment(sketch, "E100.3.0.4", {"start": v(131.76, -28.6) * mm, "end": v(147.64, -28.6) * mm});
            skLineSegment(sketch, "E100.3.0.5", {"start": v(147.64, -20.67) * mm, "end": v(147.64, -28.6) * mm});
            skLineSegment(sketch, "E100.3.0.6", {"start": v(131.76, -20.67) * mm, "end": v(147.64, -20.67) * mm});
            skLineSegment(sketch, "E100.3.0.7", {"start": v(131.76, -20.67) * mm, "end": v(131.76, -28.6) * mm});
            skCircle(sketch, "E100.3.0.8", {"center": v(139.7, -33.27) * mm, "radius": 1.27 * mm});
            skCircle(sketch, "E100.3.0.9", {"center": v(139.7, -16) * mm, "radius": 1.27 * mm});
            skLineSegment(sketch, "E100.4.0.0", {"start": v(178.56, -38.1) * mm, "end": v(202.44, -38.1) * mm, "construction": true});
            skLineSegment(sketch, "E100.4.0.1", {"start": v(202.44, -11.18) * mm, "end": v(202.44, -38.1) * mm, "construction": true});
            skLineSegment(sketch, "E100.4.0.2", {"start": v(178.56, -11.18) * mm, "end": v(202.44, -11.18) * mm, "construction": true});
            skLineSegment(sketch, "E100.4.0.3", {"start": v(178.56, -11.18) * mm, "end": v(178.56, -38.1) * mm, "construction": true});
            skLineSegment(sketch, "E100.4.0.4", {"start": v(182.56, -28.6) * mm, "end": v(198.44, -28.6) * mm});
            skLineSegment(sketch, "E100.4.0.5", {"start": v(198.44, -20.67) * mm, "end": v(198.44, -28.6) * mm});
            skLineSegment(sketch, "E100.4.0.6", {"start": v(182.56, -20.67) * mm, "end": v(198.44, -20.67) * mm});
            skLineSegment(sketch, "E100.4.0.7", {"start": v(182.56, -20.67) * mm, "end": v(182.56, -28.6) * mm});
            skCircle(sketch, "E100.4.0.8", {"center": v(190.5, -33.27) * mm, "radius": 1.27 * mm});
            skCircle(sketch, "E100.4.0.9", {"center": v(190.5, -16) * mm, "radius": 1.27 * mm});
            skLineSegment(sketch, "E100.5.0.0", {"start": v(229.36, -38.1) * mm, "end": v(253.24, -38.1) * mm, "construction": true});
            skLineSegment(sketch, "E100.5.0.1", {"start": v(253.24, -11.18) * mm, "end": v(253.24, -38.1) * mm, "construction": true});
            skLineSegment(sketch, "E100.5.0.2", {"start": v(229.36, -11.18) * mm, "end": v(253.24, -11.18) * mm, "construction": true});
            skLineSegment(sketch, "E100.5.0.3", {"start": v(229.36, -11.18) * mm, "end": v(229.36, -38.1) * mm, "construction": true});
            skLineSegment(sketch, "E100.5.0.4", {"start": v(233.36, -28.6) * mm, "end": v(249.24, -28.6) * mm});
            skLineSegment(sketch, "E100.5.0.5", {"start": v(249.24, -20.67) * mm, "end": v(249.24, -28.6) * mm});
            skLineSegment(sketch, "E100.5.0.6", {"start": v(233.36, -20.67) * mm, "end": v(249.24, -20.67) * mm});
            skLineSegment(sketch, "E100.5.0.7", {"start": v(233.36, -20.67) * mm, "end": v(233.36, -28.6) * mm});
            skCircle(sketch, "E100.5.0.8", {"center": v(241.3, -33.27) * mm, "radius": 1.27 * mm});
            skCircle(sketch, "E100.5.0.9", {"center": v(241.3, -16) * mm, "radius": 1.27 * mm});
            skLineSegment(sketch, "E100.direction1", {"start": v(-24.64, -38.1) * mm, "end": v(26.16, -38.1) * mm, "construction": true});
            skSolve(sketch);
        }
        {
            var Q0;
            Q0 = qSketchRegion(id + "F26", true);
            extrude(context, id + "F27", {"entities" : qUnion([Q0]), "operationType" : NewBodyOperationType.REMOVE, "endBound" : BoundingType.THROUGH_ALL, "oppositeDirection" : true, "depth" : 25.4 * mm});
        }
        {
            var Q0;
            Q0=makeQuery(id+"F22.opExtrude","SWEPT_EDGE",EDGE,{"disambiguationData":[OSD([sQuery(id+"F21.wireOp",EDGE,"E59.bottom"),sQuery(id+"F21.wireOp",EDGE,"E59.left")])]});
            var Q1;
            Q1=makeQuery(id+"F22.opExtrude","SWEPT_EDGE",EDGE,{"disambiguationData":[OSD([sQuery(id+"F21.wireOp",EDGE,"E59.bottom"),sQuery(id+"F21.wireOp",EDGE,"E59.right")])]});
            fillet(context, id + "F28", {"entities" : qUnion([Q0, Q1]), "radius" : 25.4 * mm, "tangentPropagation" : true, "allowEdgeOverflow" : false});
        }
        {
            var Q0;
            Q0=makeQuery(id+"F22.opExtrude","SWEPT_EDGE",EDGE,{"disambiguationData":[OSD([sQuery(id+"F21.wireOp",EDGE,"E59.top"),sQuery(id+"F21.wireOp",EDGE,"E59.left")])]});
            var Q1;
            Q1=makeQuery(id+"F22.opExtrude","SWEPT_EDGE",EDGE,{"disambiguationData":[OSD([sQuery(id+"F21.wireOp",EDGE,"E59.top"),sQuery(id+"F21.wireOp",EDGE,"E59.right")])]});
            fillet(context, id + "F29", {"entities" : qUnion([Q0, Q1]), "radius" : 9.52 * mm, "tangentPropagation" : true, "allowEdgeOverflow" : false});
        }
    });
